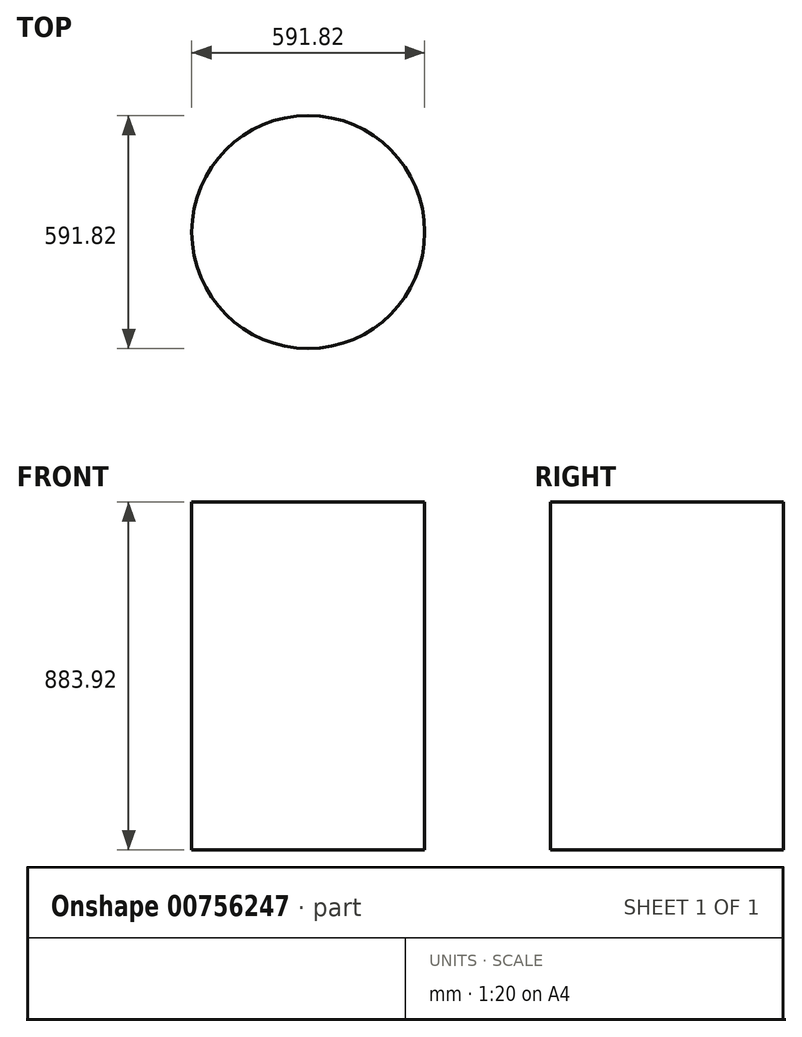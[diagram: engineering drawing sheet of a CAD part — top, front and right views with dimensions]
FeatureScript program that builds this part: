
annotation { "Feature Type Name" : "Feature", "Feature Type Description" : "" }
export const myFeature = defineFeature(function(context is Context, id is Id, definition is map)
    precondition{}
    {
        {
            var Q0;
            Q0=qCreatedBy(makeId("Front.planeOp"),FACE);
            var sketch = newSketch(context, id + "F0", { "sketchPlane" : qUnion([Q0])});
            skLineSegment(sketch, "E0.bottom", {"start": v(0, 0) * mm, "end": v(295.91, 0) * mm});
            skLineSegment(sketch, "E0.top", {"start": v(0, -883.92) * mm, "end": v(295.91, -883.92) * mm});
            skLineSegment(sketch, "E0.left", {"start": v(0, 0) * mm, "end": v(0, -883.92) * mm});
            skLineSegment(sketch, "E0.right", {"start": v(295.91, 0) * mm, "end": v(295.91, -883.92) * mm});
            skSolve(sketch);
        }
        {
            var Q0;
            Q0=makeQuery(id+"F0.imprint","IMPRINT",FACE,{"disambiguationData":[TD([[makeQuery(id+"F0.imprint","IMPRINT",EDGE,{"derivedFrom":sQuery(id+"F0.wireOp",EDGE,"E0.bottom")}),-1.0]])]});
            var Q1;
            Q1=sQuery(id+"F0.wireOp",EDGE,"E0.right");
            revolve(context, id + "F1", {"surfaceOperationType" : NewSurfaceOperationType.NEW, "entities" : qUnion([Q0]), "axis" : qUnion([Q1]), "revolveType" : RevolveType.FULL});
        }
    });
